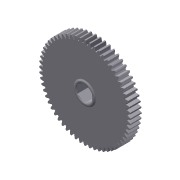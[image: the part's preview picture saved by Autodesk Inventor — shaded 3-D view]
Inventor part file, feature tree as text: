
AUTODESK INVENTOR PART (.ipt)
format: ipt  version: 2011 (Build 150239000, 239)  size: 419,840 bytes
history: native  units: mm (DEFAULTED — no unit token found)
features: sketch x5, other x4, extrude x3, plane x3, revolve x1, projected_geometry x1
ambient origin geometry x8: Origin, YZ Plane, XZ Plane, XY Plane, X Axis, Y Axis, Z Axis, Center Point
bodies: Solid1 (feature_tree)
feature tree (17):
  other  "Gear 60T 20dp 500hex"
  extrude  "Extrusion1"  Depth=9.525mm TaperAngle=0.0deg
  plane  "Work Plane1"
  plane  "Work Plane2"
  plane  "Work Plane3"
  other  "Spur Gear"
  extrude  "Extrusion2"  Depth=76.2mm TaperAngle=0.0deg
  extrude  "Extrusion3"  TaperAngle=0.0deg  [1 undecoded]
  revolve  "Revolution1"  [1 undecoded]
  sketch  "Sketch1"  dims[d0=78.74mm d1=9.525mm d2=0.0mm]
  sketch  "Sketch2"  dims[d3=76.2mm d4=76.2mm d5=0.0mm]
  other  "Srf1"
  sketch  "Sketch3"  dims[d6=0.0mm d7=0.523599mm d9=0.0mm]
  sketch  "Sketch4"  dims[d14=0.0mm d15=190.5mm d16=0.0mm]
  sketch  "Sketch5"  dims[d17=0.0mm d18=0.0mm d19=190.5mm d20=19.05mm d21=0.635mm d22=0.0mm d23=12.7mm d24=0.635mm d25=0.0mm d26=5.070181mm d27=6.35mm d28=0.889mm d29=5.070181mm d30=2.54mm d31=90.0deg]
  projected_geometry  "Projected Loop1"
  other  "Pitch Diameter"
note: 2 required parameter values undecoded (feature->parameter linkage not recoverable at this tier; creation-order binding heuristic only, values carry confidence <= 0.55)